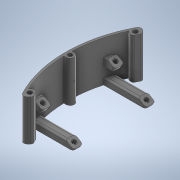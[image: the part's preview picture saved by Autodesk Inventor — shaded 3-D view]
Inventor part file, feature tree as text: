
AUTODESK INVENTOR PART (.ipt)
format: ipt  version: 2020 (Build 240168000, 168)  size: 1,408,512 bytes
history: native  units: mm
features: projected_geometry x32, extrude x20, sketch x13, other x9, fillet x1
ambient origin geometry x8: Origin, YZ Plane, XZ Plane, XY Plane, X Axis, Y Axis, Z Axis, Center Point
bodies: Body1 (feature_tree)
feature tree (75):
  other  "Твердое тело1"
  extrude  "outer"  TaperAngle=45.0deg  [1 undecoded]
  extrude  "inner"  Depth=7.0mm
  sketch  "Эскиз3"
  extrude  "Выдавливание3"  Depth=20.0mm
  extrude  "Выдавливание4"  Depth=7.0mm
  sketch  "Эскиз4"
  extrude  "Выдавливание5"  Depth=3.2mm
  extrude  "Выдавливание6"  Depth=59.0mm
  sketch  "Эскиз5"
  extrude  "Выдавливание7"  Depth=83.0mm
  extrude  "Выдавливание8"  Depth=69.0mm
  sketch  "Эскиз6"
  extrude  "Выдавливание9"  Depth=55.0mm
  extrude  "Выдавливание10"  Depth=3.0mm
  fillet  "Сопряжение1"  Radius=8.0mm
  other  "РабПлоскость2"
  other  "РабПлоскость3"
  sketch  "Эскиз10"
  sketch  "Эскиз11"
  other  "РабПлоскость4"
  other  "РабПлоскость5"
  other  "РабОсь2"
  other  "РабОсь1"
  sketch  "Эскиз12"
  extrude  "Выдавливание12"  Depth=5.0mm
  sketch  "Эскиз8"
  extrude  "asterisk"  Depth=2.0mm
  other  "РабПлоскость7"
  sketch  "Эскиз13"
  extrude  "Выдавливание13"  Depth=40.0mm TaperAngle=360.0deg
  extrude  "Выдавливание14"  Depth=2.0mm
  extrude  "Выдавливание15"  Depth=105.0mm
  extrude  "Выдавливание17"  Depth=2.0mm
  extrude  "Выдавливание18"  Depth=2.0mm TaperAngle=0.0deg
  extrude  "Выдавливание16"  Depth=3.5mm
  extrude  "Выдавливание19"  Depth=2.0mm
  extrude  "Выдавливание20"  Depth=6.0mm
  sketch  "Эскиз1"
  sketch  "Эскиз2"
  projected_geometry  "Спроецированная петля1"
  projected_geometry  "Спроецированная петля2"
  projected_geometry  "Спроецированная петля3"
  projected_geometry  "Спроецированная петля4"
  projected_geometry  "Спроецированная петля5"
  projected_geometry  "Спроецированная петля8"
  projected_geometry  "Спроецированная петля9"
  projected_geometry  "Спроецированная петля10"
  projected_geometry  "Спроецированная петля11"
  projected_geometry  "Спроецированная петля12"
  other  "РабПлоскость6"
  projected_geometry  "Спроецированная петля13"
  projected_geometry  "Спроецированная петля14"
  projected_geometry  "Спроецированная петля15"
  projected_geometry  "Спроецированная петля16"
  projected_geometry  "Спроецированная петля17"
  projected_geometry  "Спроецированная петля18"
  projected_geometry  "Спроецированная петля19"
  projected_geometry  "Спроецированная петля20"
  projected_geometry  "Спроецированная петля21"
  projected_geometry  "Спроецированная петля22"
  projected_geometry  "Спроецированная петля23"
  projected_geometry  "Спроецированная петля24"
  projected_geometry  "Спроецированная петля25"
  projected_geometry  "Спроецированная петля26"
  projected_geometry  "Спроецированная петля27"
  projected_geometry  "Спроецированная петля28"
  projected_geometry  "Спроецированная петля29"
  projected_geometry  "Спроецированная петля30"
  projected_geometry  "Спроецированная петля31"
  projected_geometry  "Спроецированная петля32"
  sketch  "Эскиз14"
  projected_geometry  "Спроецированная петля33"
  sketch  "Эскиз15"
  projected_geometry  "Спроецированная петля34"
note: 1 required parameter value undecoded (feature->parameter linkage not recoverable at this tier; creation-order binding heuristic only, values carry confidence <= 0.55)
